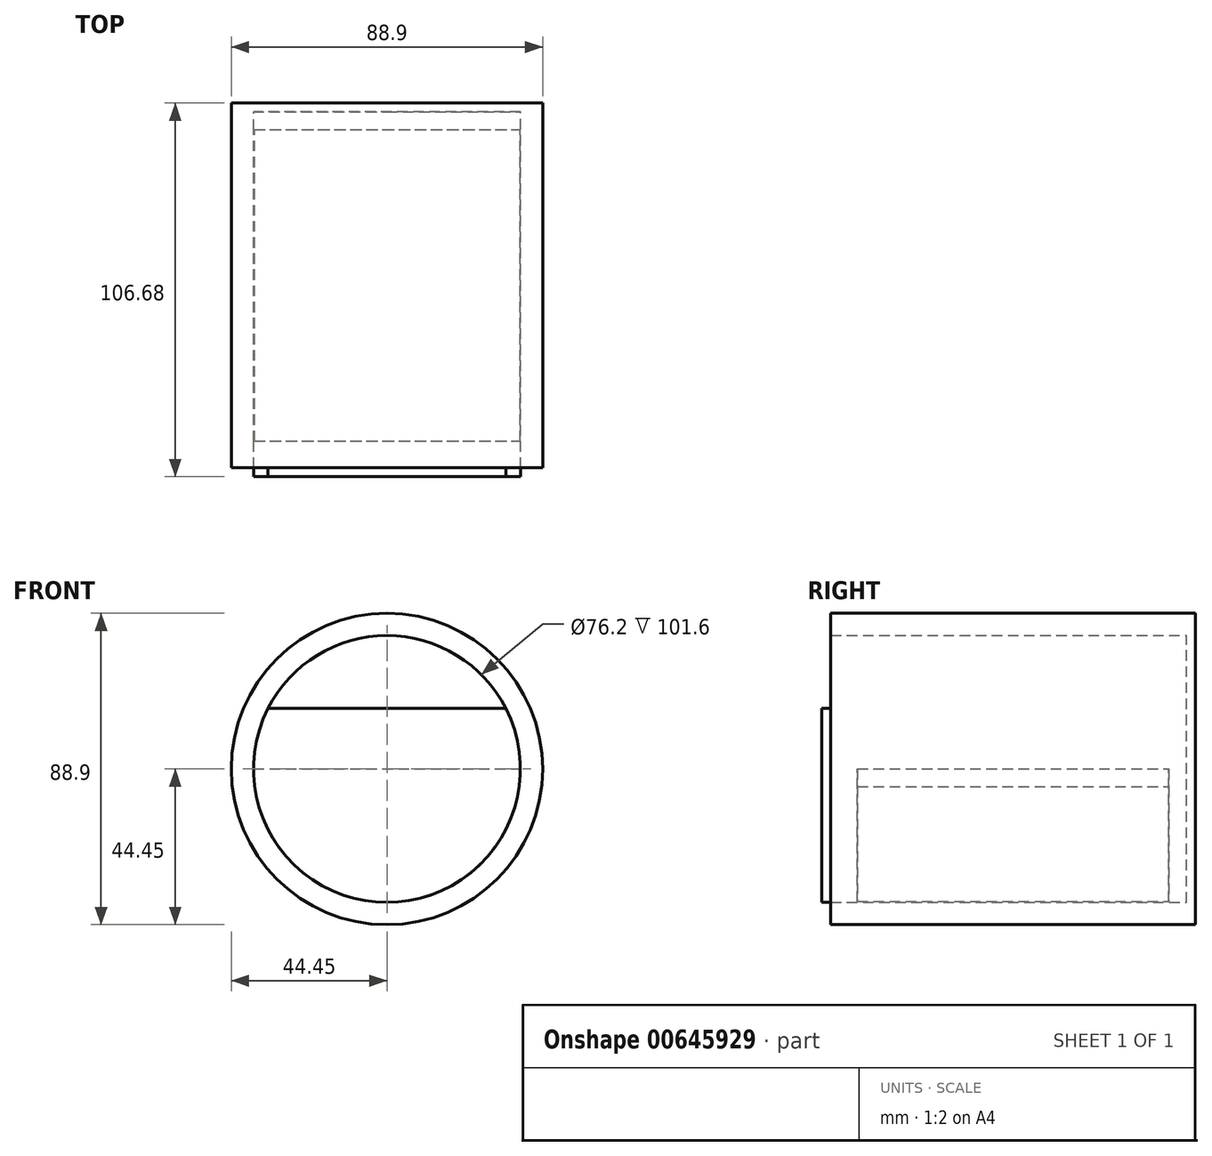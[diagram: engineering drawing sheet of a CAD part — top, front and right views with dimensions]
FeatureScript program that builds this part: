
annotation { "Feature Type Name" : "Feature", "Feature Type Description" : "" }
export const myFeature = defineFeature(function(context is Context, id is Id, definition is map)
    precondition{}
    {
        {
            var Q0;
            Q0=qCreatedBy(makeId("Front.planeOp"),FACE);
            var sketch = newSketch(context, id + "F0", { "sketchPlane" : qUnion([Q0])});
            skCircle(sketch, "E0", {"center": v(0, 0) * mm, "radius": 38.1 * mm});
            skCircle(sketch, "E1", {"center": v(0, 0) * mm, "radius": 44.45 * mm});
            skSolve(sketch);
        }
        {
            var Q0;
            Q0 = qSketchRegion(id + "F0", true);
            extrude(context, id + "F1", {"entities" : qUnion([Q0]), "depth" : 101.6 * mm, "offsetDistance" : 25.4 * mm});
        }
        {
            var Q0;
            Q0=qCreatedBy(makeId("Front.planeOp"),FACE);
            var sketch = newSketch(context, id + "F2", { "sketchPlane" : qUnion([Q0])});
            skCircle(sketch, "E2", {"center": v(0, 0) * mm, "radius": 44.45 * mm});
            skSolve(sketch);
        }
        {
            var Q0;
            Q0 = qSketchRegion(id + "F2", true);
            extrude(context, id + "F3", {"entities" : qUnion([Q0]), "operationType" : NewBodyOperationType.ADD, "oppositeDirection" : true, "depth" : 2.54 * mm, "offsetDistance" : 25.4 * mm});
        }
        {
            var Q0;
            Q0=qCreatedBy(makeId("Front.planeOp"),FACE);
            cPlane(context, id + "F4", {"entities" : qUnion([Q0]), "cplaneType" : CPlaneType.OFFSET, "offset" : 5.08 * mm, "width" : 152.4 * mm, "height" : 152.4 * mm});
        }
        {
            var Q0;
            Q0=qCreatedBy(id+"F4.planeOp",FACE);
            var sketch = newSketch(context, id + "F5", { "sketchPlane" : qUnion([Q0])});
            skLineSegment(sketch, "E3", {"start": v(-38.13, 0) * mm, "end": v(38.07, 0) * mm});
            skArc(sketch, "E4", {"start": v(-38.13, 0) * mm, "mid": v(-0.03, -37.85) * mm, "end": v(38.07, 0) * mm});
            skSolve(sketch);
        }
        {
            var Q0;
            Q0=makeQuery(id+"F5.imprint","IMPRINT",FACE,{"disambiguationData":[TD([[makeQuery(id+"F5.imprint","IMPRINT",EDGE,{"derivedFrom":sQuery(id+"F5.wireOp",EDGE,"E3")}),-1.0]])]});
            extrude(context, id + "F6", {"entities" : qUnion([Q0]), "operationType" : NewBodyOperationType.ADD, "depth" : 88.9 * mm, "offsetDistance" : 25.4 * mm});
        }
        {
            var Q0;
            Q0=makeQuery(id+"F1.opExtrude","CAP_FACE",FACE,{"disambiguationData":[OSD([sQuery(id+"F0.wireOp",EDGE,"E0"),sQuery(id+"F0.wireOp",EDGE,"E1")])],"isStart":false});
            var sketch = newSketch(context, id + "F7", { "sketchPlane" : qUnion([Q0])});
            skLineSegment(sketch, "E5", {"start": v(-40.96, 17.27) * mm, "end": v(40.96, 17.27) * mm});
            skArc(sketch, "E6", {"start": v(-40.96, 17.27) * mm, "mid": v(0, -39.29) * mm, "end": v(40.96, 17.27) * mm});
            skSolve(sketch);
        }
        {
            var Q0;
            {var subQ0=sQuery(id+"F7.wireOp",EDGE,"E5");var subQ1=makeQuery(id+"F1.opExtrude","CAP_EDGE",EDGE,{"disambiguationData":[OSD([sQuery(id+"F0.wireOp",EDGE,"E0")])],"isStart":false});var subQ2=makeQuery(id+"F7.imprint","INTERSECT",VERTEX,{"disambiguationData":[OD(0.0)],"derivedFrom":[subQ1,subQ0]});Q0=makeQuery(id+"F7.imprint","IMPRINT",FACE,{"disambiguationData":[TD([[makeQuery(id+"F7.imprint","IMPRINT",EDGE,{"disambiguationData":[TD([[subQ2,-1.0]])],"derivedFrom":subQ0}),-1.0]])]});}
            extrude(context, id + "F8", {"entities" : qUnion([Q0]), "depth" : 2.54 * mm, "offsetDistance" : 25.4 * mm});
        }
    });
